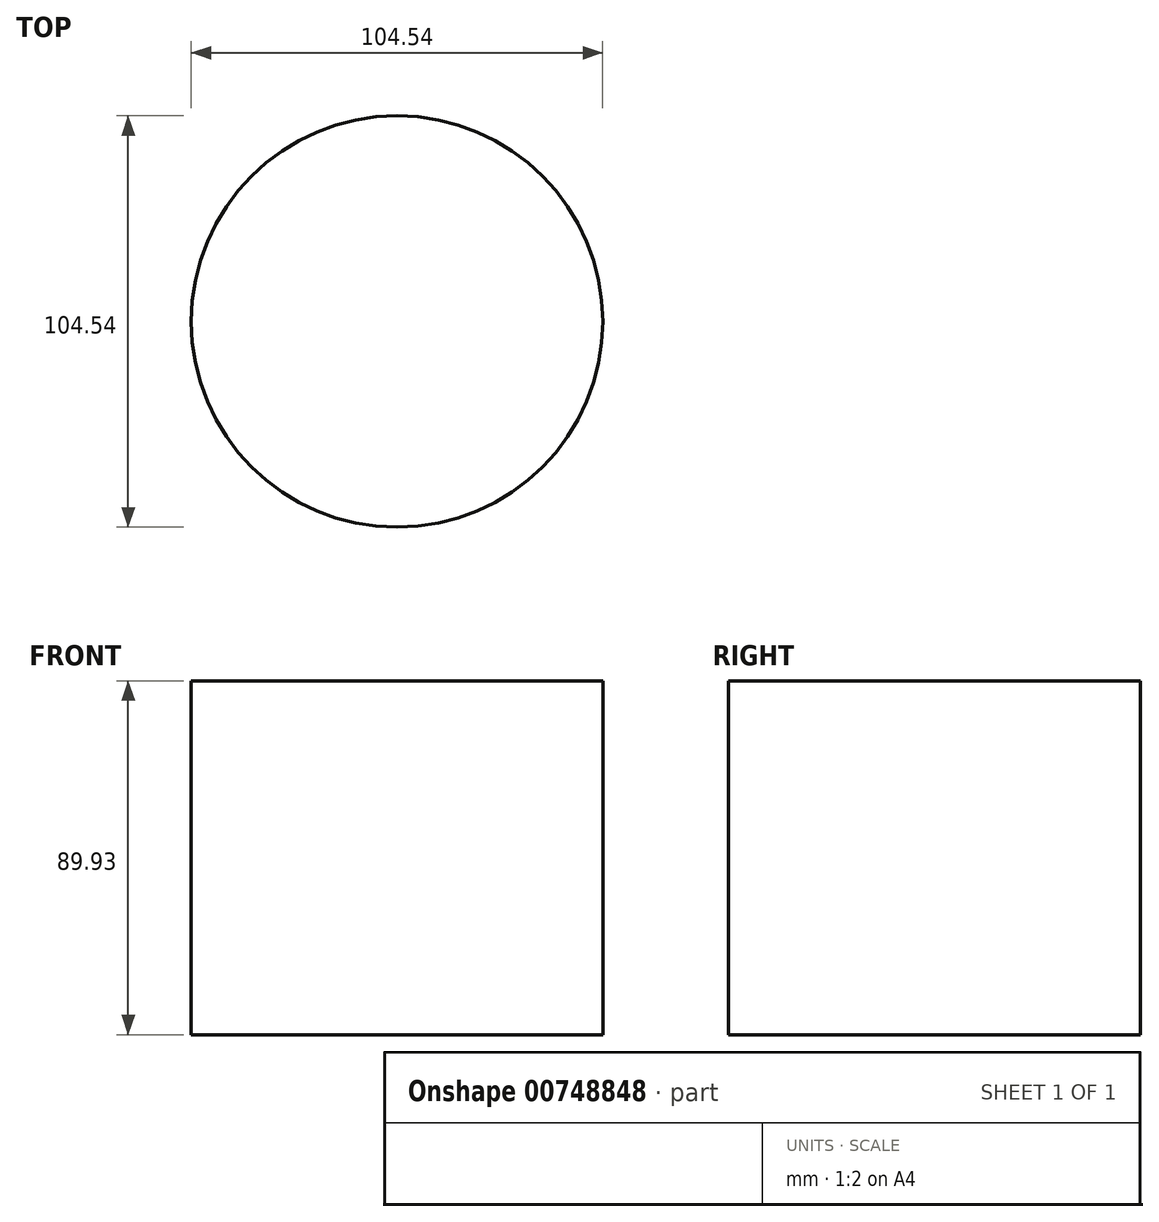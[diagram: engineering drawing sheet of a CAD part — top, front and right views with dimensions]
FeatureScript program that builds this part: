
annotation { "Feature Type Name" : "Feature", "Feature Type Description" : "" }
export const myFeature = defineFeature(function(context is Context, id is Id, definition is map)
    precondition{}
    {
        {
            var Q0;
            Q0=qCreatedBy(makeId("Top.planeOp"),FACE);
            var sketch = newSketch(context, id + "F0", { "sketchPlane" : qUnion([Q0])});
            skCircle(sketch, "E0", {"center": v(0, 0) * mm, "radius": 52.27 * mm});
            skSolve(sketch);
        }
        {
            var Q0;
            Q0=makeQuery(id+"F0.imprint","IMPRINT",FACE,{"disambiguationData":[TD([[makeQuery(id+"F0.imprint","IMPRINT",EDGE,{"derivedFrom":sQuery(id+"F0.wireOp",EDGE,"E0")}),1.0]])]});
            extrude(context, id + "F1", {"entities" : qUnion([Q0]), "depth" : 89.93 * mm, "offsetDistance" : 25.4 * mm});
        }
    });
